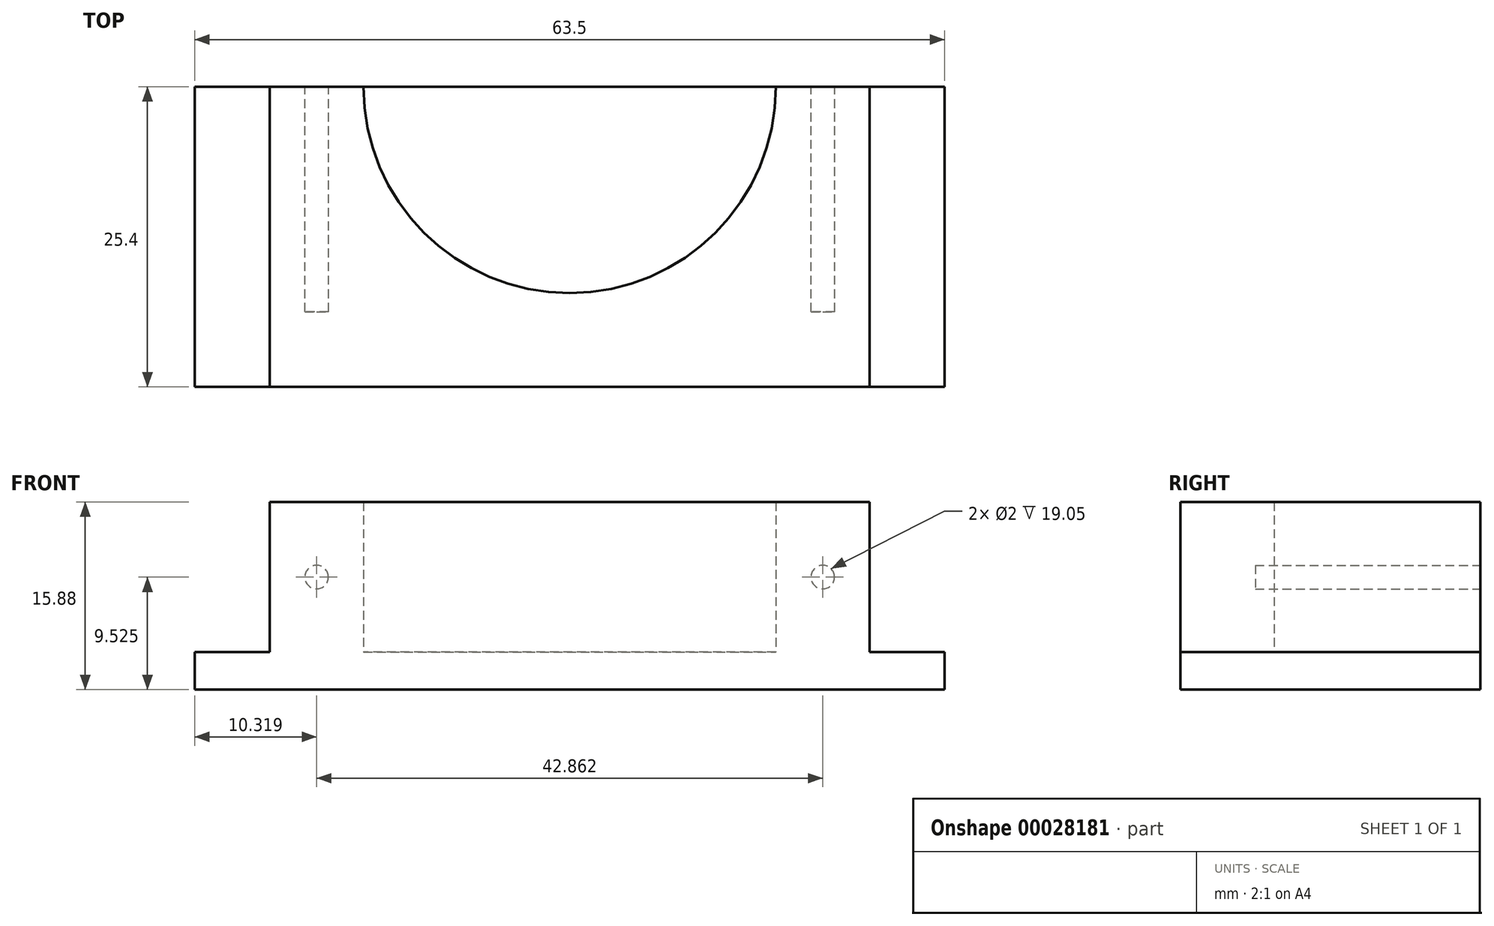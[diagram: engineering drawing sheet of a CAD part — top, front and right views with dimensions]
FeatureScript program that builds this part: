
annotation { "Feature Type Name" : "Feature", "Feature Type Description" : "" }
export const myFeature = defineFeature(function(context is Context, id is Id, definition is map)
    precondition{}
    {
        {
            var Q0;
            Q0=qCreatedBy(makeId("Top.planeOp"),FACE);
            var sketch = newSketch(context, id + "F0", { "sketchPlane" : qUnion([Q0])});
            skLineSegment(sketch, "E0.rect.bottom", {"start": v(31.75, 12.7) * mm, "end": v(-31.75, 12.7) * mm});
            skLineSegment(sketch, "E0.rect.top", {"start": v(31.75, -12.7) * mm, "end": v(-31.75, -12.7) * mm});
            skLineSegment(sketch, "E0.rect.left", {"start": v(31.75, 12.7) * mm, "end": v(31.75, -12.7) * mm});
            skLineSegment(sketch, "E0.rect.right", {"start": v(-31.75, 12.7) * mm, "end": v(-31.75, -12.7) * mm});
            skPoint(sketch, "E0.rect.middle", {"position": v(0, 0) * mm});
            skSolve(sketch);
        }
        {
            var Q0;
            Q0=makeQuery(id+"F0.imprint","IMPRINT",FACE,{"disambiguationData":[TD([[makeQuery(id+"F0.imprint","IMPRINT",EDGE,{"derivedFrom":sQuery(id+"F0.wireOp",EDGE,"E0.rect.bottom")}),1.0]])]});
            extrude(context, id + "F1", {"entities" : qUnion([Q0]), "depth" : 3.17 * mm});
        }
        {
            var Q0;
            Q0=makeQuery(id+"F1.opExtrude","CAP_FACE",FACE,{"disambiguationData":[OSD([sQuery(id+"F0.wireOp",EDGE,"E0.rect.bottom"),sQuery(id+"F0.wireOp",EDGE,"E0.rect.top"),sQuery(id+"F0.wireOp",EDGE,"E0.rect.left"),sQuery(id+"F0.wireOp",EDGE,"E0.rect.right")])],"isStart":false});
            var sketch = newSketch(context, id + "F2", { "sketchPlane" : qUnion([Q0])});
            skPoint(sketch, "E1.rect.middle", {"position": v(0, 0) * mm});
            skPoint(sketch, "E2", {"position": v(-17.46, 12.7) * mm});
            skPoint(sketch, "E3", {"position": v(17.46, 12.7) * mm});
            skArc(sketch, "E4", {"start": v(-17.46, 12.7) * mm, "mid": v(0, -4.76) * mm, "end": v(17.46, 12.7) * mm});
            skLineSegment(sketch, "E5", {"start": v(17.46, 12.7) * mm, "end": v(25.4, 12.7) * mm});
            skLineSegment(sketch, "E6", {"start": v(-25.4, 12.7) * mm, "end": v(-25.4, -12.7) * mm});
            skLineSegment(sketch, "E7", {"start": v(25.4, 12.7) * mm, "end": v(25.4, -12.7) * mm});
            skLineSegment(sketch, "E8", {"start": v(-25.4, -12.7) * mm, "end": v(25.4, -12.7) * mm});
            skLineSegment(sketch, "E9", {"start": v(-25.4, 12.7) * mm, "end": v(-17.46, 12.7) * mm});
            skSolve(sketch);
        }
        {
            var Q0;
            Q0 = qSketchRegion(id + "F2", true);
            extrude(context, id + "F3", {"entities" : qUnion([Q0]), "operationType" : NewBodyOperationType.ADD, "depth" : 12.7 * mm});
        }
        {
            var Q0;
            Q0=makeQuery(id+"F3.boolean.opBoolean","MERGE",FACE,{"derivedFrom":[makeQuery(id+"F1.opExtrude","SWEPT_FACE",FACE,{"disambiguationData":[OSD([sQuery(id+"F0.wireOp",EDGE,"E0.rect.bottom")])]}),makeQuery(id+"F3.opExtrude","SWEPT_FACE",FACE,{"disambiguationData":[OSD([sQuery(id+"F2.wireOp",EDGE,"E5")])]}),makeQuery(id+"F3.opExtrude","SWEPT_FACE",FACE,{"disambiguationData":[OSD([sQuery(id+"F2.wireOp",EDGE,"E9")])]})]});
            var sketch = newSketch(context, id + "F4", { "sketchPlane" : qUnion([Q0])});
            skLineSegment(sketch, "E10", {"start": v(-21.43, 15.88) * mm, "end": v(-21.43, 0) * mm, "construction": true});
            skLineSegment(sketch, "E11", {"start": v(21.43, 15.88) * mm, "end": v(21.43, 0) * mm, "construction": true});
            skCircle(sketch, "E12", {"center": v(-21.43, 9.52) * mm, "radius": 1 * mm});
            skCircle(sketch, "E13", {"center": v(21.43, 9.52) * mm, "radius": 1 * mm});
            skSolve(sketch);
        }
        {
            var Q0;
            Q0 = qSketchRegion(id + "F4", true);
            extrude(context, id + "F5", {"entities" : qUnion([Q0]), "operationType" : NewBodyOperationType.REMOVE, "oppositeDirection" : true, "depth" : 19.05 * mm});
        }
    });
